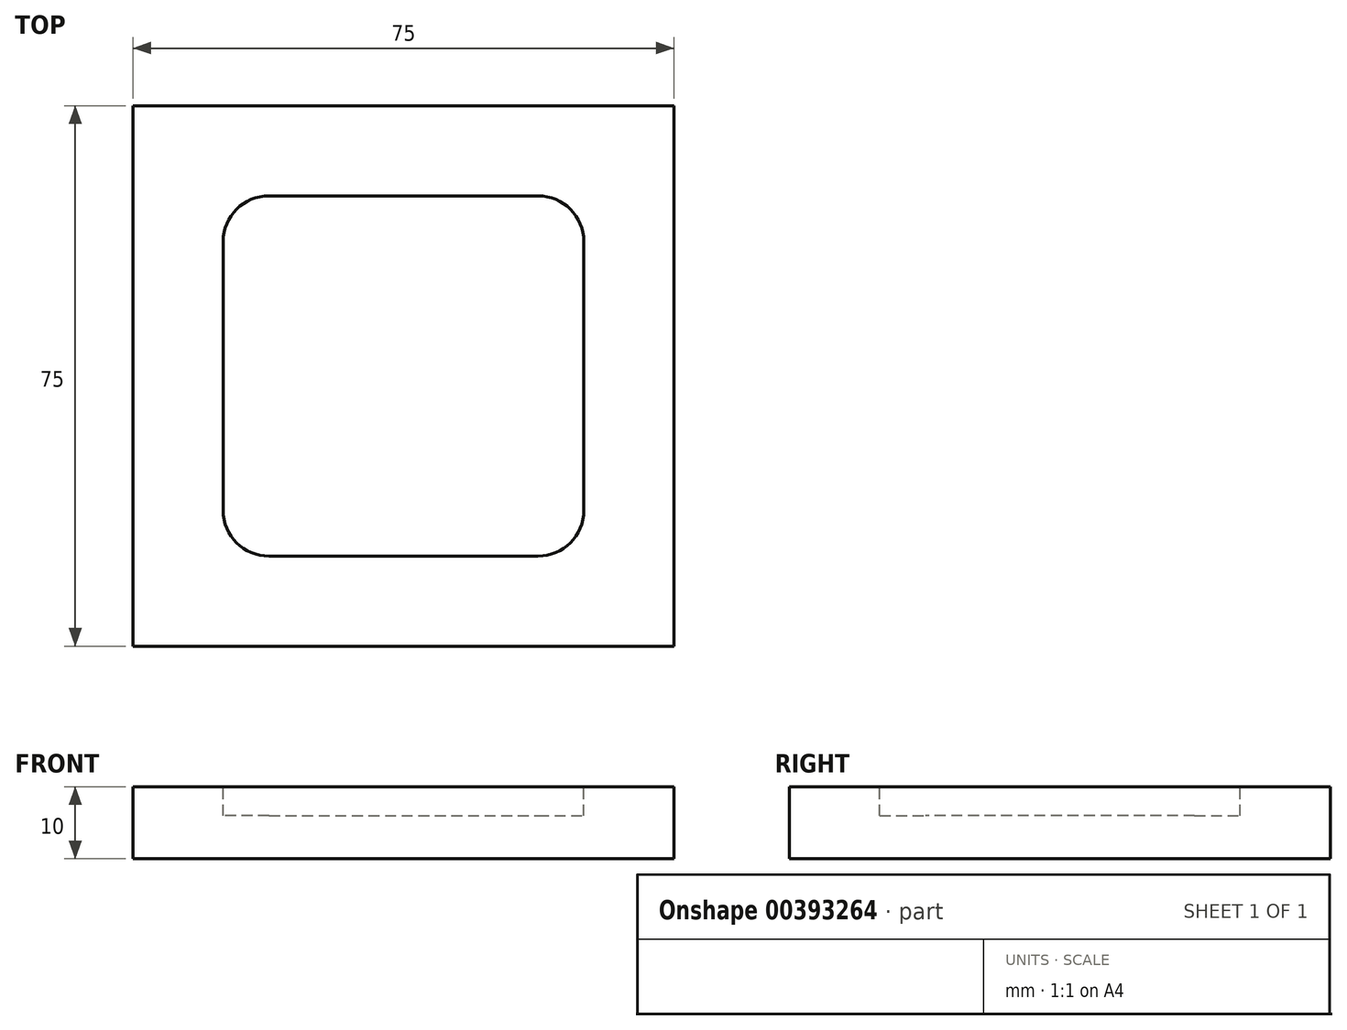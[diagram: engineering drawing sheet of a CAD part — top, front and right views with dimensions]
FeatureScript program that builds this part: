
annotation { "Feature Type Name" : "Feature", "Feature Type Description" : "" }
export const myFeature = defineFeature(function(context is Context, id is Id, definition is map)
    precondition{}
    {
        {
            var Q0;
            Q0=qCreatedBy(makeId("Top.planeOp"),FACE);
            var sketch = newSketch(context, id + "F0", { "sketchPlane" : qUnion([Q0])});
            skLineSegment(sketch, "E0.bottom", {"start": v(-37.5, 37.5) * mm, "end": v(37.5, 37.5) * mm});
            skLineSegment(sketch, "E0.top", {"start": v(-37.5, -37.5) * mm, "end": v(37.5, -37.5) * mm});
            skLineSegment(sketch, "E0.left", {"start": v(-37.5, 37.5) * mm, "end": v(-37.5, -37.5) * mm});
            skLineSegment(sketch, "E0.right", {"start": v(37.5, 37.5) * mm, "end": v(37.5, -37.5) * mm});
            skPoint(sketch, "E0.middle", {"position": v(0, 0) * mm});
            skSolve(sketch);
        }
        {
            var Q0;
            Q0 = qSketchRegion(id + "F0", true);
            extrude(context, id + "F1", {"entities" : qUnion([Q0]), "depth" : 10 * mm});
        }
        {
            var Q0;
            Q0=makeQuery(id+"F1.opExtrude","CAP_FACE",FACE,{"disambiguationData":[OSD([sQuery(id+"F0.wireOp",EDGE,"E0.bottom"),sQuery(id+"F0.wireOp",EDGE,"E0.top"),sQuery(id+"F0.wireOp",EDGE,"E0.left"),sQuery(id+"F0.wireOp",EDGE,"E0.right")])],"isStart":false});
            var sketch = newSketch(context, id + "F2", { "sketchPlane" : qUnion([Q0])});
            skLineSegment(sketch, "E1.bottom", {"start": v(-25, 25) * mm, "end": v(25, 25) * mm});
            skLineSegment(sketch, "E1.top", {"start": v(-25, -25) * mm, "end": v(25, -25) * mm});
            skLineSegment(sketch, "E1.left", {"start": v(-25, 25) * mm, "end": v(-25, -25) * mm});
            skLineSegment(sketch, "E1.right", {"start": v(25, 25) * mm, "end": v(25, -25) * mm});
            skPoint(sketch, "E1.middle", {"position": v(0, 0) * mm});
            skSolve(sketch);
        }
        {
            var Q0;
            Q0 = qSketchRegion(id + "F2", true);
            extrude(context, id + "F3", {"entities" : qUnion([Q0]), "operationType" : NewBodyOperationType.REMOVE, "oppositeDirection" : true, "depth" : 4 * mm});
        }
        {
            var Q0;
            Q0=makeQuery(id+"F3.boolean.opBoolean","COPY",EDGE,{"derivedFrom":makeQuery(id+"F3.opExtrude","SWEPT_EDGE",EDGE,{"disambiguationData":[OSD([sQuery(id+"F2.wireOp",EDGE,"E1.bottom"),sQuery(id+"F2.wireOp",EDGE,"E1.left")])]})});
            var Q1;
            Q1=makeQuery(id+"F3.boolean.opBoolean","COPY",EDGE,{"derivedFrom":makeQuery(id+"F3.opExtrude","SWEPT_EDGE",EDGE,{"disambiguationData":[OSD([sQuery(id+"F2.wireOp",EDGE,"E1.bottom"),sQuery(id+"F2.wireOp",EDGE,"E1.right")])]})});
            var Q2;
            Q2=makeQuery(id+"F3.boolean.opBoolean","COPY",EDGE,{"derivedFrom":makeQuery(id+"F3.opExtrude","SWEPT_EDGE",EDGE,{"disambiguationData":[OSD([sQuery(id+"F2.wireOp",EDGE,"E1.top"),sQuery(id+"F2.wireOp",EDGE,"E1.left")])]})});
            var Q3;
            Q3=makeQuery(id+"F3.boolean.opBoolean","COPY",EDGE,{"derivedFrom":makeQuery(id+"F3.opExtrude","SWEPT_EDGE",EDGE,{"disambiguationData":[OSD([sQuery(id+"F2.wireOp",EDGE,"E1.top"),sQuery(id+"F2.wireOp",EDGE,"E1.right")])]})});
            fillet(context, id + "F4", {"entities" : qUnion([Q0, Q1, Q2, Q3]), "radius" : 6.35 * mm, "tangentPropagation" : true, "allowEdgeOverflow" : false});
        }
    });
